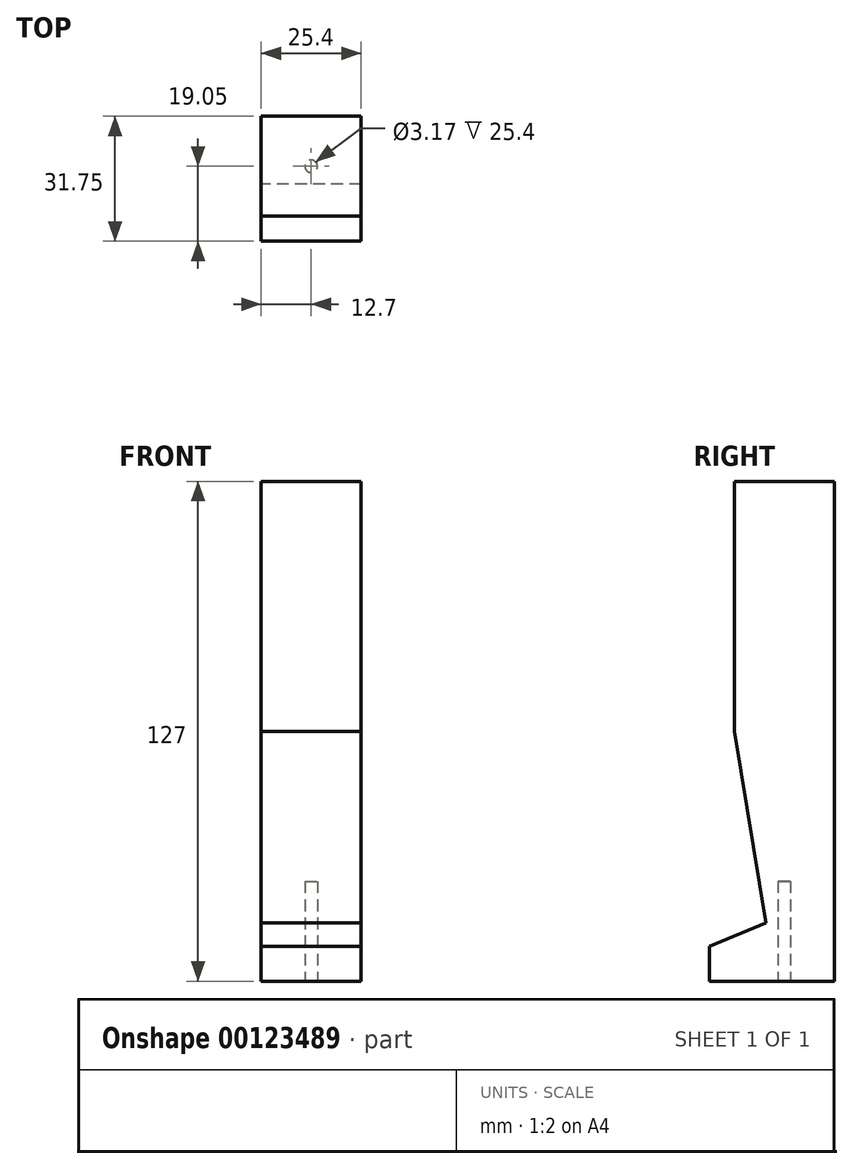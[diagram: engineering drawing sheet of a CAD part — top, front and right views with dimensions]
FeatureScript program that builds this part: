
annotation { "Feature Type Name" : "Feature", "Feature Type Description" : "" }
export const myFeature = defineFeature(function(context is Context, id is Id, definition is map)
    precondition{}
    {
        {
            var Q0;
            Q0=qCreatedBy(makeId("Right.planeOp"),FACE);
            var sketch = newSketch(context, id + "F0", { "sketchPlane" : qUnion([Q0])});
            skLineSegment(sketch, "E0", {"start": v(-12.7, 0) * mm, "end": v(-12.7, 63.5) * mm});
            skLineSegment(sketch, "E1", {"start": v(-12.7, 63.5) * mm, "end": v(12.7, 63.5) * mm});
            skLineSegment(sketch, "E2", {"start": v(12.7, 63.5) * mm, "end": v(12.7, 0) * mm});
            skLineSegment(sketch, "E3", {"start": v(12.7, 0) * mm, "end": v(12.7, -63.5) * mm});
            skLineSegment(sketch, "E4", {"start": v(12.7, -63.5) * mm, "end": v(-19.05, -63.5) * mm});
            skLineSegment(sketch, "E5", {"start": v(-19.05, -63.5) * mm, "end": v(-19.05, -54.6) * mm});
            skLineSegment(sketch, "E6", {"start": v(-19.05, -54.6) * mm, "end": v(-4.57, -48.67) * mm});
            skLineSegment(sketch, "E7", {"start": v(-4.57, -48.67) * mm, "end": v(-12.7, 0) * mm});
            skLineSegment(sketch, "E8", {"start": v(-12.7, 0) * mm, "end": v(12.7, 0) * mm, "construction": true});
            skSolve(sketch);
        }
        {
            var Q0;
            Q0=qSketchRegion(id+"F0",true);
            extrude(context, id + "F1", {"entities" : qUnion([Q0]), "depth" : 25.4 * mm});
        }
        {
            var Q0;
            Q0=makeQuery(id+"F1.opExtrude","SWEPT_FACE",FACE,{"disambiguationData":[OSD([sQuery(id+"F0.wireOp",EDGE,"E4")])]});
            var sketch = newSketch(context, id + "F2", { "sketchPlane" : qUnion([Q0])});
            skCircle(sketch, "E9", {"center": v(12.7, 0) * mm, "radius": 1.59 * mm});
            skLineSegment(sketch, "E10", {"start": v(12.7, -12.7) * mm, "end": v(12.7, 0) * mm, "construction": true});
            skSolve(sketch);
        }
        {
            var Q0;
            Q0 = qSketchRegion(id + "F2", true);
            extrude(context, id + "F3", {"entities" : qUnion([Q0]), "operationType" : NewBodyOperationType.REMOVE, "oppositeDirection" : true, "depth" : 25.4 * mm});
        }
    });
